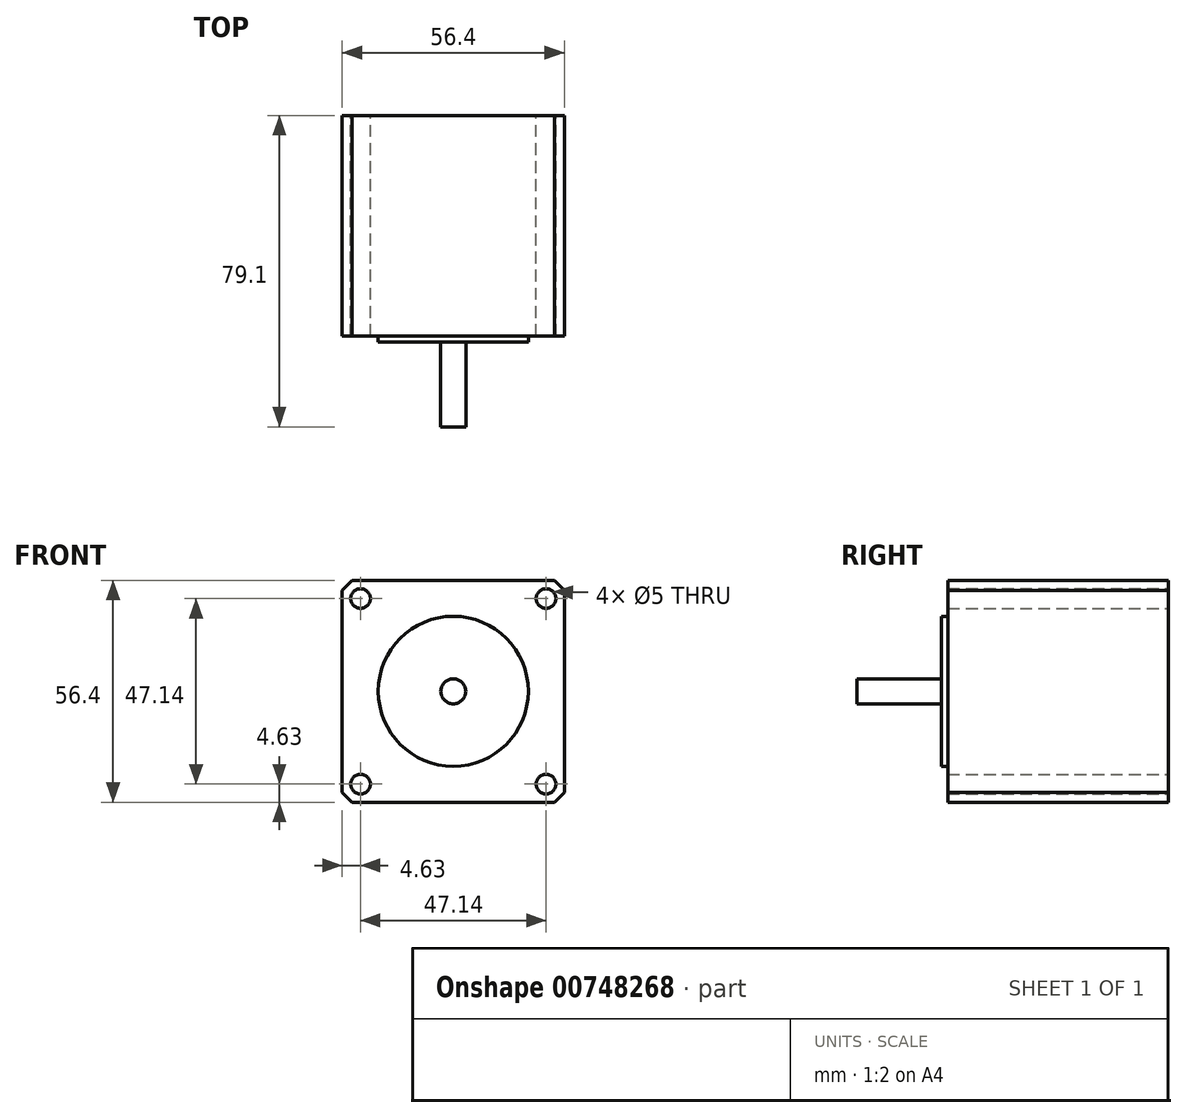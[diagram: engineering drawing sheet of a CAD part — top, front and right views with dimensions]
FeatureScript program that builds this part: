
annotation { "Feature Type Name" : "Feature", "Feature Type Description" : "" }
export const myFeature = defineFeature(function(context is Context, id is Id, definition is map)
    precondition{}
    {
        {
            var Q0;
            Q0=qCreatedBy(makeId("Front.planeOp"),FACE);
            var sketch = newSketch(context, id + "F0", { "sketchPlane" : qUnion([Q0])});
            skLineSegment(sketch, "E0.bottom", {"start": v(28.2, -28.2) * mm, "end": v(-28.2, -28.2) * mm});
            skLineSegment(sketch, "E0.top", {"start": v(28.2, 28.2) * mm, "end": v(-28.2, 28.2) * mm});
            skLineSegment(sketch, "E0.left", {"start": v(28.2, -28.2) * mm, "end": v(28.2, 28.2) * mm});
            skLineSegment(sketch, "E0.right", {"start": v(-28.2, -28.2) * mm, "end": v(-28.2, 28.2) * mm});
            skPoint(sketch, "E0.middle", {"position": v(0, 0) * mm});
            skSolve(sketch);
        }
        {
            var Q0;
            Q0 = qSketchRegion(id + "F0", true);
            extrude(context, id + "F1", {"entities" : qUnion([Q0]), "depth" : 56 * mm, "offsetDistance" : 25.4 * mm});
        }
        {
            var Q0;
            Q0=makeQuery(id+"F1.opExtrude","CAP_FACE",FACE,{"disambiguationData":[OSD([sQuery(id+"F0.wireOp",EDGE,"E0.bottom"),sQuery(id+"F0.wireOp",EDGE,"E0.top"),sQuery(id+"F0.wireOp",EDGE,"E0.left"),sQuery(id+"F0.wireOp",EDGE,"E0.right")])],"isStart":false});
            var sketch = newSketch(context, id + "F2", { "sketchPlane" : qUnion([Q0])});
            skCircle(sketch, "E1", {"center": v(0, 0) * mm, "radius": 19.05 * mm});
            skSolve(sketch);
        }
        {
            var Q0;
            Q0 = qSketchRegion(id + "F2", true);
            extrude(context, id + "F3", {"entities" : qUnion([Q0]), "operationType" : NewBodyOperationType.ADD, "depth" : 1.6 * mm, "offsetDistance" : 25.4 * mm});
        }
        {
            var Q0;
            Q0=makeQuery(id+"F3.opExtrude","CAP_FACE",FACE,{"disambiguationData":[OSD([sQuery(id+"F2.wireOp",EDGE,"E1")])],"isStart":false});
            var sketch = newSketch(context, id + "F4", { "sketchPlane" : qUnion([Q0])});
            skCircle(sketch, "E2", {"center": v(0, 0) * mm, "radius": 3.17 * mm});
            skSolve(sketch);
        }
        {
            var Q0;
            Q0 = qSketchRegion(id + "F4", true);
            extrude(context, id + "F5", {"entities" : qUnion([Q0]), "operationType" : NewBodyOperationType.ADD, "depth" : 21.5 * mm, "offsetDistance" : 25.4 * mm});
        }
        {
            var Q0;
            Q0=makeQuery(id+"F1.opExtrude","CAP_FACE",FACE,{"disambiguationData":[OSD([sQuery(id+"F0.wireOp",EDGE,"E0.bottom"),sQuery(id+"F0.wireOp",EDGE,"E0.top"),sQuery(id+"F0.wireOp",EDGE,"E0.left"),sQuery(id+"F0.wireOp",EDGE,"E0.right")])],"isStart":true});
            var sketch = newSketch(context, id + "F6", { "sketchPlane" : qUnion([Q0])});
            skLineSegment(sketch, "E3.bottom", {"start": v(23.57, -23.57) * mm, "end": v(-23.57, -23.57) * mm, "construction": true});
            skLineSegment(sketch, "E3.top", {"start": v(23.57, 23.57) * mm, "end": v(-23.57, 23.57) * mm, "construction": true});
            skLineSegment(sketch, "E3.left", {"start": v(23.57, -23.57) * mm, "end": v(23.57, 23.57) * mm, "construction": true});
            skLineSegment(sketch, "E3.right", {"start": v(-23.57, -23.57) * mm, "end": v(-23.57, 23.57) * mm, "construction": true});
            skPoint(sketch, "E3.middle", {"position": v(0, 0) * mm});
            skCircle(sketch, "E4", {"center": v(23.57, 23.57) * mm, "radius": 2.5 * mm});
            skCircle(sketch, "E5", {"center": v(23.57, -23.57) * mm, "radius": 2.5 * mm});
            skCircle(sketch, "E6", {"center": v(-23.57, -23.57) * mm, "radius": 2.5 * mm});
            skCircle(sketch, "E7", {"center": v(-23.57, 23.57) * mm, "radius": 2.5 * mm});
            skSolve(sketch);
        }
        {
            var Q0;
            Q0 = qSketchRegion(id + "F6", true);
            extrude(context, id + "F7", {"entities" : qUnion([Q0]), "operationType" : NewBodyOperationType.REMOVE, "endBound" : BoundingType.THROUGH_ALL, "oppositeDirection" : true, "depth" : 25.4 * mm, "offsetDistance" : 25.4 * mm});
        }
        {
            var Q0;
            Q0=makeQuery(id+"F1.opExtrude","SWEPT_EDGE",EDGE,{"disambiguationData":[OSD([sQuery(id+"F0.wireOp",EDGE,"E0.top"),sQuery(id+"F0.wireOp",EDGE,"E0.left")])]});
            var Q1;
            Q1=makeQuery(id+"F1.opExtrude","SWEPT_EDGE",EDGE,{"disambiguationData":[OSD([sQuery(id+"F0.wireOp",EDGE,"E0.top"),sQuery(id+"F0.wireOp",EDGE,"E0.right")])]});
            var Q2;
            Q2=makeQuery(id+"F1.opExtrude","SWEPT_EDGE",EDGE,{"disambiguationData":[OSD([sQuery(id+"F0.wireOp",EDGE,"E0.bottom"),sQuery(id+"F0.wireOp",EDGE,"E0.right")])]});
            var Q3;
            Q3=makeQuery(id+"F1.opExtrude","SWEPT_EDGE",EDGE,{"disambiguationData":[OSD([sQuery(id+"F0.wireOp",EDGE,"E0.bottom"),sQuery(id+"F0.wireOp",EDGE,"E0.left")])]});
            chamfer(context, id + "F8", {"entities" : qUnion([Q0, Q1, Q2, Q3]), "width" : 2.54 * mm, "tangentPropagation" : true});
        }
    });
